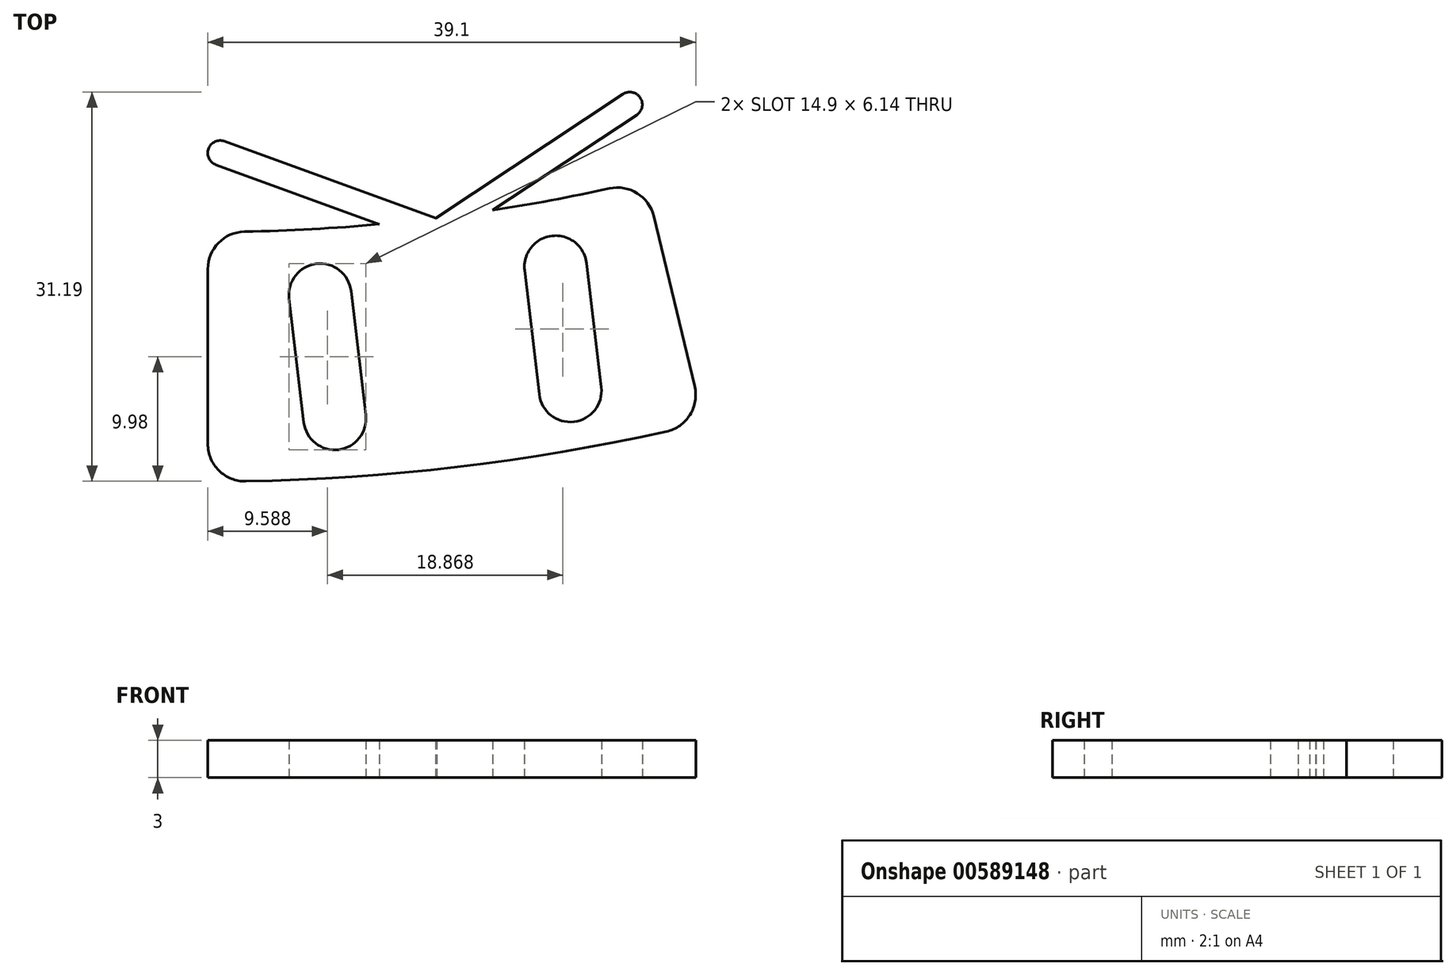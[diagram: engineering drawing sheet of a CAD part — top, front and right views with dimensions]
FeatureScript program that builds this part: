
annotation { "Feature Type Name" : "Feature", "Feature Type Description" : "" }
export const myFeature = defineFeature(function(context is Context, id is Id, definition is map)
    precondition{}
    {
        {
            var Q0;
            Q0=qCreatedBy(makeId("Top.planeOp"),FACE);
            var sketch = newSketch(context, id + "F0", { "sketchPlane" : qUnion([Q0])});
            skArc(sketch, "E0", {"start": v(2.94, -149.97) * mm, "mid": v(8.35, -149.77) * mm, "end": v(13.74, -149.37) * mm});
            skArc(sketch, "E1", {"start": v(3.05, -169.97) * mm, "mid": v(20, -168.82) * mm, "end": v(36.75, -165.98) * mm});
            skLineSegment(sketch, "E2", {"start": v(0, -152.97) * mm, "end": v(0, -166.97) * mm});
            skLineSegment(sketch, "E3", {"start": v(0, -166.97) * mm, "end": v(0, -152.97) * mm});
            skLineSegment(sketch, "E4", {"start": v(35.74, -148.74) * mm, "end": v(39.01, -162.35) * mm});
            skPoint(sketch, "E5.visualSharp", {"position": v(0, -150) * mm});
            skArc(sketch, "E5.filletArc", {"start": v(2.94, -149.97) * mm, "mid": v(0.86, -150.87) * mm, "end": v(0, -152.97) * mm});
            skPoint(sketch, "E6.visualSharp", {"position": v(0, -170) * mm});
            skArc(sketch, "E6.filletArc", {"start": v(0, -166.97) * mm, "mid": v(0.9, -169.11) * mm, "end": v(3.05, -169.97) * mm});
            skPoint(sketch, "E7.visualSharp", {"position": v(35.05, -145.85) * mm});
            skArc(sketch, "E7.filletArc", {"start": v(35.74, -148.74) * mm, "mid": v(34.42, -146.9) * mm, "end": v(32.18, -146.5) * mm});
            skPoint(sketch, "E8.visualSharp", {"position": v(39.72, -165.3) * mm});
            skArc(sketch, "E8.filletArc", {"start": v(36.75, -165.98) * mm, "mid": v(38.64, -164.64) * mm, "end": v(39.01, -162.35) * mm});
            skLineSegment(sketch, "E9", {"start": v(18.26, -148.88) * mm, "end": v(33.26, -138.95) * mm});
            skLineSegment(sketch, "E10", {"start": v(34.37, -140.61) * mm, "end": v(22.84, -148.25) * mm});
            skLineSegment(sketch, "E11", {"start": v(18.26, -148.88) * mm, "end": v(1.34, -142.73) * mm});
            skLineSegment(sketch, "E12", {"start": v(0, -143.67) * mm, "end": v(0, -143.67) * mm});
            skLineSegment(sketch, "E13.trimOffspring", {"start": v(34.79, -139.54) * mm, "end": v(34.79, -139.54) * mm});
            skArc(sketch, "E14.trimOffspring", {"start": v(22.84, -148.25) * mm, "mid": v(27.52, -147.45) * mm, "end": v(32.18, -146.5) * mm});
            skLineSegment(sketch, "E15.trimOffspring", {"start": v(18.33, -148.88) * mm, "end": v(18.28, -148.87) * mm});
            skLineSegment(sketch, "E16", {"start": v(0.66, -144.6) * mm, "end": v(13.74, -149.37) * mm});
            skArc(sketch, "E17.trimOffspring", {"start": v(18.26, -148.88) * mm, "mid": v(18.3, -148.88) * mm, "end": v(18.33, -148.88) * mm});
            skPoint(sketch, "E18.orphan", {"position": v(0, -165) * mm});
            skPoint(sketch, "E19.trimOffspring.end.orphan", {"position": v(37.2, -154.82) * mm});
            skPoint(sketch, "E20.visualSharp", {"position": v(0, -142.24) * mm});
            skArc(sketch, "E20.filletArc", {"start": v(1.34, -142.73) * mm, "mid": v(0.43, -142.85) * mm, "end": v(0, -143.67) * mm});
            skPoint(sketch, "E21.visualSharp", {"position": v(0, -144.37) * mm});
            skArc(sketch, "E21.filletArc", {"start": v(0, -143.67) * mm, "mid": v(0.18, -144.24) * mm, "end": v(0.66, -144.6) * mm});
            skPoint(sketch, "E22.visualSharp", {"position": v(34.44, -138.17) * mm});
            skArc(sketch, "E22.filletArc", {"start": v(34.79, -139.54) * mm, "mid": v(34.18, -138.85) * mm, "end": v(33.26, -138.95) * mm});
            skPoint(sketch, "E23.visualSharp", {"position": v(34.96, -140.22) * mm});
            skArc(sketch, "E23.filletArc", {"start": v(34.37, -140.61) * mm, "mid": v(34.75, -140.14) * mm, "end": v(34.79, -139.54) * mm});
            skPoint(sketch, "E24.center.orphan", {"position": v(9.14, -164.77) * mm});
            skArc(sketch, "E25", {"start": v(11.48, -154.73) * mm, "mid": v(8.7, -152.54) * mm, "end": v(6.52, -155.32) * mm});
            skArc(sketch, "E26", {"start": v(30.35, -152.5) * mm, "mid": v(27.57, -150.3) * mm, "end": v(25.39, -153.08) * mm});
            skArc(sketch, "E27", {"start": v(7.7, -165.25) * mm, "mid": v(10.47, -167.44) * mm, "end": v(12.66, -164.66) * mm});
            skArc(sketch, "E28", {"start": v(26.56, -163.01) * mm, "mid": v(29.34, -165.2) * mm, "end": v(31.53, -162.43) * mm});
            skLineSegment(sketch, "E29", {"start": v(6.52, -155.32) * mm, "end": v(7.7, -165.25) * mm});
            skLineSegment(sketch, "E30", {"start": v(12.66, -164.66) * mm, "end": v(11.48, -154.73) * mm});
            skLineSegment(sketch, "E31", {"start": v(25.39, -153.08) * mm, "end": v(26.56, -163.01) * mm});
            skLineSegment(sketch, "E32", {"start": v(31.53, -162.43) * mm, "end": v(30.35, -152.5) * mm});
            skSolve(sketch);
        }
        {
            var Q0;
            Q0=makeQuery(id+"F0.imprint","IMPRINT",FACE,{"disambiguationData":[TD([[makeQuery(id+"F0.imprint","IMPRINT",EDGE,{"derivedFrom":sQuery(id+"F0.wireOp",EDGE,"E1")}),1.0]])]});
            var Q1;
            {var subQ1=sQuery(id+"F0.wireOp",EDGE,"E20.filletArc");Q1=makeQuery(id+"F0.imprint","IMPRINT",FACE,{"disambiguationData":[TD([[makeQuery(id+"F0.imprint","IMPRINT",EDGE,{"derivedFrom":subQ1}),1.0]])]});}
            extrude(context, id + "F1", {"entities" : qUnion([Q0, Q1]), "depth" : 3 * mm, "offsetDistance" : 25 * mm});
        }
    });
